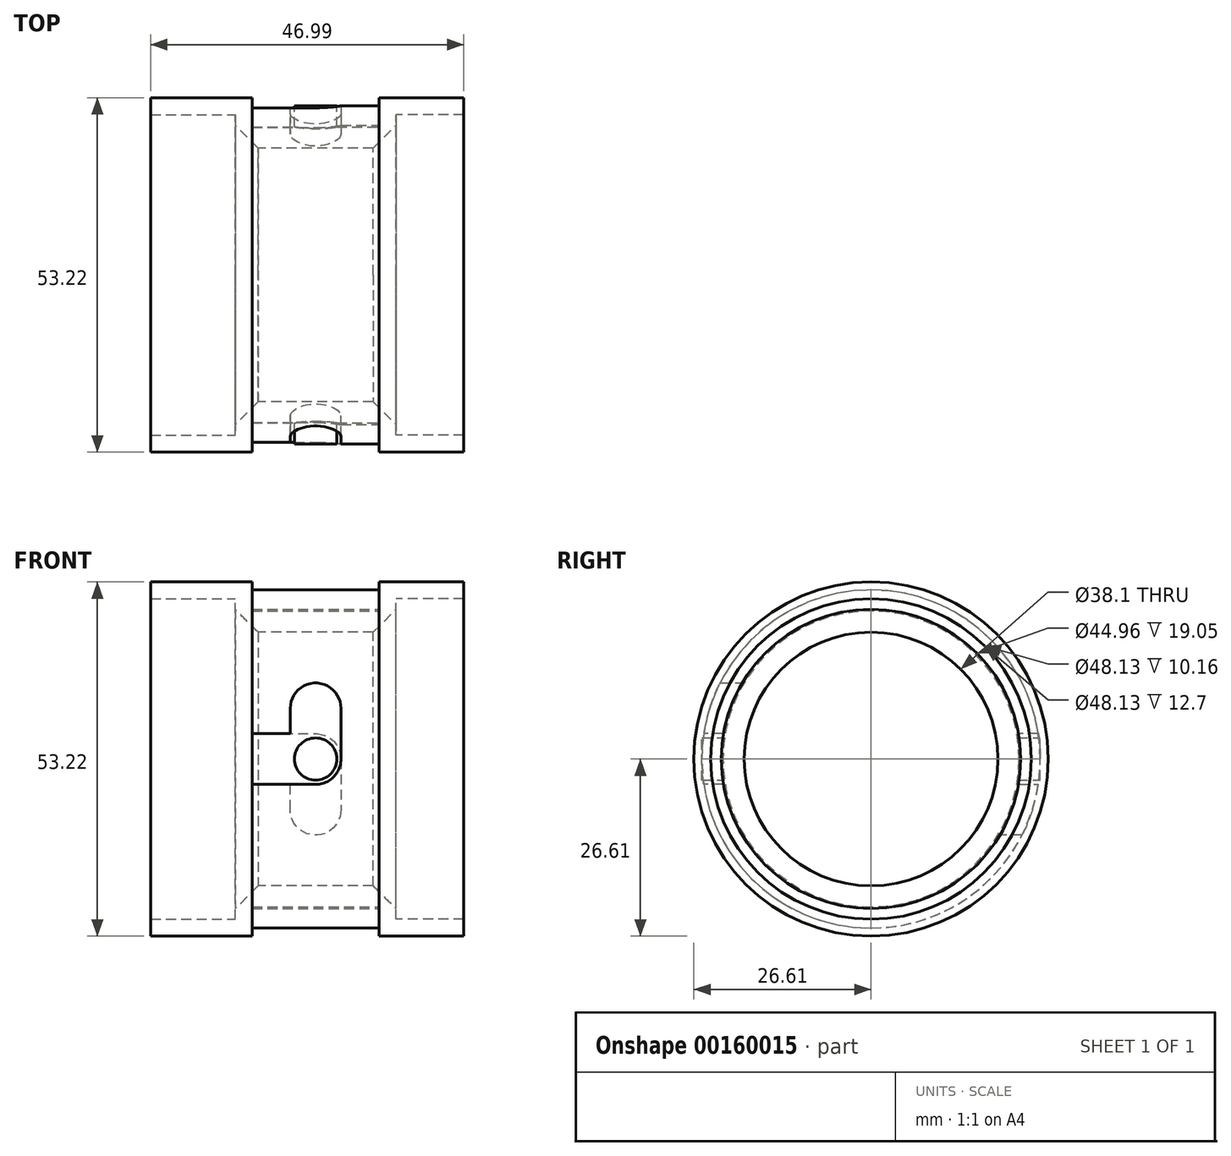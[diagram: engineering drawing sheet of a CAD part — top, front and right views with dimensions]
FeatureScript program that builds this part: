
annotation { "Feature Type Name" : "Feature", "Feature Type Description" : "" }
export const myFeature = defineFeature(function(context is Context, id is Id, definition is map)
    precondition{}
    {
        {
            var Q0;
            Q0=qCreatedBy(makeId("Right.planeOp"),FACE);
            var sketch = newSketch(context, id + "F0", { "sketchPlane" : qUnion([Q0])});
            skCircle(sketch, "E0", {"center": v(0, 0) * mm, "radius": 24.07 * mm});
            skCircle(sketch, "E1", {"center": v(0, 0) * mm, "radius": 26.6 * mm});
            skCircle(sketch, "E2", {"center": v(0, 0) * mm, "radius": 19.05 * mm});
            skSolve(sketch);
        }
        {
            var Q0;
            Q0=makeQuery(id+"F0.imprint","IMPRINT",FACE,{"disambiguationData":[TD([[makeQuery(id+"F0.imprint","IMPRINT",EDGE,{"derivedFrom":sQuery(id+"F0.wireOp",EDGE,"E0")}),-1.0]])]});
            var Q1;
            Q1=makeQuery(id+"F0.imprint","IMPRINT",FACE,{"disambiguationData":[TD([[makeQuery(id+"F0.imprint","IMPRINT",EDGE,{"derivedFrom":sQuery(id+"F0.wireOp",EDGE,"E0")}),1.0]])]});
            extrude(context, id + "F1", {"entities" : qUnion([Q0, Q1]), "depth" : 2.54 * mm});
        }
        {
            var Q0;
            Q0=makeQuery(id+"F0.imprint","IMPRINT",FACE,{"disambiguationData":[TD([[makeQuery(id+"F0.imprint","IMPRINT",EDGE,{"derivedFrom":sQuery(id+"F0.wireOp",EDGE,"E0")}),-1.0]])]});
            extrude(context, id + "F2", {"entities" : qUnion([Q0]), "operationType" : NewBodyOperationType.ADD, "depth" : 12.7 * mm});
        }
        {
            var Q0;
            Q0=qCreatedBy(makeId("Right.planeOp"),FACE);
            var sketch = newSketch(context, id + "F3", { "sketchPlane" : qUnion([Q0])});
            skCircle(sketch, "E3", {"center": v(0, 0) * mm, "radius": 22.48 * mm});
            skCircle(sketch, "E4", {"center": v(0, 0) * mm, "radius": 25.4 * mm});
            skSolve(sketch);
        }
        {
            var Q0;
            Q0 = qSketchRegion(id + "F3", true);
            extrude(context, id + "F4", {"entities" : qUnion([Q0]), "operationType" : NewBodyOperationType.ADD, "oppositeDirection" : true, "offsetDistance" : 25.4 * mm, "depth" : 19.05 * mm});
        }
        {
            var Q0;
            Q0=qCreatedBy(makeId("Front.planeOp"),FACE);
            var sketch = newSketch(context, id + "F5", { "sketchPlane" : qUnion([Q0])});
            skLineSegment(sketch, "E5", {"start": v(0, 0) * mm, "end": v(-19.05, 0) * mm, "construction": true});
            skLineSegment(sketch, "E6", {"start": v(-19.05, -3.81) * mm, "end": v(-19.05, 3.8) * mm});
            skLineSegment(sketch, "E7", {"start": v(-19.05, 3.8) * mm, "end": v(-9.53, 3.8) * mm});
            skLineSegment(sketch, "E8", {"start": v(-9.53, 3.8) * mm, "end": v(-9.52, -3.8) * mm});
            skLineSegment(sketch, "E9", {"start": v(-9.52, -3.81) * mm, "end": v(-19.05, -3.81) * mm});
            skSolve(sketch);
        }
        {
            var Q0;
            Q0=qSketchRegion(id+"F5",true);
            extrude(context, id + "F6", {"entities" : qUnion([Q0]), "operationType" : NewBodyOperationType.REMOVE, "oppositeDirection" : true, "depth" : 50.8 * mm, "hasSecondDirection" : true, "secondDirectionOppositeDirection" : false, "secondDirectionDepth" : 50.8 * mm});
        }
        {
            var Q0;
            Q0=qCreatedBy(makeId("Front.planeOp"),FACE);
            var sketch = newSketch(context, id + "F7", { "sketchPlane" : qUnion([Q0])});
            skLineSegment(sketch, "E10", {"start": v(0, 0) * mm, "end": v(-9.53, 0) * mm, "construction": true});
            skCircle(sketch, "E11", {"center": v(-9.53, 0) * mm, "radius": 3.81 * mm});
            skSolve(sketch);
        }
        {
            var Q0;
            Q0=qSketchRegion(id+"F7",true);
            extrude(context, id + "F8", {"entities" : qUnion([Q0]), "operationType" : NewBodyOperationType.REMOVE, "oppositeDirection" : true, "depth" : 50.8 * mm, "hasSecondDirection" : true, "secondDirectionOppositeDirection" : false, "secondDirectionDepth" : 50.8 * mm});
        }
        {
            var Q0;
            Q0=qCreatedBy(makeId("Front.planeOp"),FACE);
            var sketch = newSketch(context, id + "F9", { "sketchPlane" : qUnion([Q0])});
            skLineSegment(sketch, "E12", {"start": v(0, 0) * mm, "end": v(-9.53, 0) * mm, "construction": true});
            skLineSegment(sketch, "E13", {"start": v(-9.53, 0) * mm, "end": v(-9.53, 7.62) * mm, "construction": true});
            skCircle(sketch, "E14", {"center": v(-9.53, 7.62) * mm, "radius": 3.81 * mm});
            skLineSegment(sketch, "E15", {"start": v(-9.53, 7.62) * mm, "end": v(-13.34, 7.62) * mm, "construction": true});
            skLineSegment(sketch, "E16", {"start": v(-13.34, 7.62) * mm, "end": v(-13.34, 0) * mm});
            skLineSegment(sketch, "E17", {"start": v(-13.34, 0) * mm, "end": v(-5.72, 0) * mm});
            skLineSegment(sketch, "E18", {"start": v(-5.72, 0) * mm, "end": v(-5.72, 7.62) * mm});
            skSolve(sketch);
        }
        {
            var Q0;
            {var subQ0=sQuery(id+"F9.wireOp",EDGE,"E14");var subQ1=makeQuery(id+"F9.imprint","INTERSECT",VERTEX,{"derivedFrom":[subQ0,sQuery(id+"F9.wireOp",EDGE,"E16")]});Q0=makeQuery(id+"F9.imprint","IMPRINT",FACE,{"disambiguationData":[TD([[makeQuery(id+"F9.imprint","IMPRINT",EDGE,{"disambiguationData":[TD([[subQ1,1.0]])],"derivedFrom":subQ0}),1.0]])]});}
            var Q1;
            {var subQ0=sQuery(id+"F9.wireOp",EDGE,"E16");Q1=makeQuery(id+"F9.imprint","IMPRINT",FACE,{"disambiguationData":[TD([[makeQuery(id+"F9.imprint","IMPRINT",EDGE,{"derivedFrom":subQ0}),1.0]])]});}
            var Q2;
            Q2=sQuery(id+"F9.wireOp",EDGE,"E15");
            extrude(context, id + "F10", {"entities" : qUnion([Q0, Q1]), "operationType" : NewBodyOperationType.REMOVE, "surfaceEntities" : qUnion([Q2]), "depth" : 50.8 * mm});
        }
        {
            var Q0;
            Q0=qCreatedBy(makeId("Front.planeOp"),FACE);
            var sketch = newSketch(context, id + "F11", { "sketchPlane" : qUnion([Q0])});
            skLineSegment(sketch, "E19", {"start": v(0, 0) * mm, "end": v(-9.53, 0) * mm, "construction": true});
            skLineSegment(sketch, "E20", {"start": v(-9.53, 0) * mm, "end": v(-9.53, -7.62) * mm, "construction": true});
            skCircle(sketch, "E21", {"center": v(-9.53, -7.62) * mm, "radius": 3.81 * mm});
            skLineSegment(sketch, "E22", {"start": v(-9.53, -7.62) * mm, "end": v(-13.33, -7.62) * mm, "construction": true});
            skLineSegment(sketch, "E23", {"start": v(-13.33, -7.62) * mm, "end": v(-13.33, 0) * mm});
            skLineSegment(sketch, "E24", {"start": v(-13.33, 0) * mm, "end": v(-5.72, 0) * mm});
            skLineSegment(sketch, "E25", {"start": v(-5.71, 0) * mm, "end": v(-5.71, -7.62) * mm});
            skSolve(sketch);
        }
        {
            var Q0;
            {var subQ0=sQuery(id+"F11.wireOp",EDGE,"E23");Q0=makeQuery(id+"F11.imprint","IMPRINT",FACE,{"disambiguationData":[TD([[makeQuery(id+"F11.imprint","IMPRINT",EDGE,{"derivedFrom":subQ0}),-1.0]])]});}
            var Q1;
            {var subQ0=sQuery(id+"F11.wireOp",EDGE,"E21");var subQ1=makeQuery(id+"F11.imprint","INTERSECT",VERTEX,{"derivedFrom":[subQ0,sQuery(id+"F11.wireOp",EDGE,"E23")]});Q1=makeQuery(id+"F11.imprint","IMPRINT",FACE,{"disambiguationData":[TD([[makeQuery(id+"F11.imprint","IMPRINT",EDGE,{"disambiguationData":[TD([[subQ1,1.0]])],"derivedFrom":subQ0}),1.0]])]});}
            var Q2;
            Q2=sQuery(id+"F11.wireOp",EDGE,"E22");
            extrude(context, id + "F12", {"entities" : qUnion([Q0, Q1]), "operationType" : NewBodyOperationType.REMOVE, "surfaceEntities" : qUnion([Q2]), "oppositeDirection" : true, "depth" : 25.4 * mm});
        }
        {
            var Q0;
            Q0=qCreatedBy(makeId("Right.planeOp"),FACE);
            var sketch = newSketch(context, id + "F13", { "sketchPlane" : qUnion([Q0])});
            skCircle(sketch, "E26", {"center": v(0, 0) * mm, "radius": 19.05 * mm});
            skCircle(sketch, "E27", {"center": v(0, 0) * mm, "radius": 22.23 * mm});
            skCircle(sketch, "E28", {"center": v(0, 0) * mm, "radius": 24.07 * mm});
            skSolve(sketch);
        }
        {
            var Q0;
            Q0=makeQuery(id+"F13.imprint","IMPRINT",FACE,{"disambiguationData":[TD([[makeQuery(id+"F13.imprint","IMPRINT",EDGE,{"derivedFrom":sQuery(id+"F13.wireOp",EDGE,"E26")}),-1.0]])]});
            extrude(context, id + "F14", {"entities" : qUnion([Q0]), "oppositeDirection" : true, "depth" : 21.59 * mm});
        }
        {
            var Q0;
            Q0=makeQuery(id+"F13.imprint","IMPRINT",FACE,{"disambiguationData":[TD([[makeQuery(id+"F13.imprint","IMPRINT",EDGE,{"derivedFrom":sQuery(id+"F13.wireOp",EDGE,"E27")}),-1.0]])]});
            extrude(context, id + "F15", {"entities" : qUnion([Q0]), "operationType" : NewBodyOperationType.ADD, "oppositeDirection" : true, "depth" : 21.59 * mm, "hasSecondDirection" : true, "secondDirectionOppositeDirection" : true, "secondDirectionDepth" : 19.05 * mm});
        }
        {
            var Q0;
            Q0=qCreatedBy(makeId("Right.planeOp"),FACE);
            var sketch = newSketch(context, id + "F16", { "sketchPlane" : qUnion([Q0])});
            skCircle(sketch, "E29", {"center": v(0, 0) * mm, "radius": 24.07 * mm});
            skCircle(sketch, "E30", {"center": v(0, 0) * mm, "radius": 26.6 * mm});
            skSolve(sketch);
        }
        {
            var Q0;
            Q0=qSketchRegion(id+"F16",true);
            extrude(context, id + "F17", {"entities" : qUnion([Q0]), "operationType" : NewBodyOperationType.ADD, "oppositeDirection" : true, "depth" : 34.3 * mm, "hasSecondDirection" : true, "secondDirectionOppositeDirection" : true, "secondDirectionDepth" : 19.05 * mm});
        }
        {
            var Q0;
            Q0=qCreatedBy(makeId("Front.planeOp"),FACE);
            var sketch = newSketch(context, id + "F18", { "sketchPlane" : qUnion([Q0])});
            skLineSegment(sketch, "E31", {"start": v(0, 0) * mm, "end": v(-9.52, 0) * mm, "construction": true});
            skCircle(sketch, "E32", {"center": v(-9.52, 0) * mm, "radius": 3.18 * mm});
            skSolve(sketch);
        }
        {
            var Q0;
            Q0=qSketchRegion(id+"F18",true);
            extrude(context, id + "F19", {"entities" : qUnion([Q0]), "operationType" : NewBodyOperationType.ADD, "depth" : 25.4 * mm, "hasSecondDirection" : true, "secondDirectionOppositeDirection" : true, "secondDirectionDepth" : 25.4 * mm});
        }
        {
            var Q0;
            Q0=makeQuery(id+"F13.imprint","IMPRINT",FACE,{"disambiguationData":[TD([[makeQuery(id+"F13.imprint","IMPRINT",EDGE,{"derivedFrom":sQuery(id+"F13.wireOp",EDGE,"E26")}),1.0]])]});
            extrude(context, id + "F20", {"entities" : qUnion([Q0]), "operationType" : NewBodyOperationType.REMOVE, "oppositeDirection" : true, "depth" : 25.4 * mm});
        }
        {
            var Q0;
            Q0=qCreatedBy(makeId("Front.planeOp"),FACE);
            var sketch = newSketch(context, id + "F21", { "sketchPlane" : qUnion([Q0])});
            skLineSegment(sketch, "E33", {"start": v(0, 0) * mm, "end": v(24.47, 0) * mm, "construction": true});
            skLineSegment(sketch, "E34", {"start": v(0, 0) * mm, "end": v(0, -22.48) * mm, "construction": true});
            skLineSegment(sketch, "E35", {"start": v(0, 0) * mm, "end": v(0, -19.94) * mm, "construction": true});
            skLineSegment(sketch, "E36", {"start": v(0, -22.48) * mm, "end": v(2.54, -22.48) * mm, "construction": true});
            skLineSegment(sketch, "E37", {"start": v(2.54, -22.48) * mm, "end": v(2.54, -19.94) * mm});
            skLineSegment(sketch, "E38", {"start": v(2.54, -19.94) * mm, "end": v(0, -19.94) * mm});
            skLineSegment(sketch, "E39", {"start": v(0, -19.94) * mm, "end": v(2.54, -22.48) * mm});
            skLineSegment(sketch, "E40", {"start": v(0, -19.94) * mm, "end": v(0, -19.05) * mm});
            skLineSegment(sketch, "E41", {"start": v(0, -19.05) * mm, "end": v(2.54, -19.05) * mm});
            skLineSegment(sketch, "E42", {"start": v(2.54, -19.05) * mm, "end": v(2.54, -19.94) * mm});
            skLineSegment(sketch, "E43", {"start": v(0, -19.94) * mm, "end": v(-0.89, -19.05) * mm});
            skLineSegment(sketch, "E44", {"start": v(-0.89, -19.05) * mm, "end": v(0, -19.05) * mm});
            skLineSegment(sketch, "E45", {"start": v(0, -19.05) * mm, "end": v(0, -19.94) * mm});
            skSolve(sketch);
        }
        {
            var Q0;
            Q0=qSketchRegion(id+"F21",true);
            var Q1;
            Q1=sQuery(id+"F21.wireOp",EDGE,"E33");
            revolve(context, id + "F22", {"operationType" : NewBodyOperationType.REMOVE, "entities" : qUnion([Q0]), "axis" : qUnion([Q1]), "revolveType" : RevolveType.FULL, "oppositeDirection" : true});
        }
        {
            var Q0;
            Q0=qCreatedBy(makeId("Front.planeOp"),FACE);
            var sketch = newSketch(context, id + "F23", { "sketchPlane" : qUnion([Q0])});
            skLineSegment(sketch, "E46", {"start": v(0, 0) * mm, "end": v(-21.59, 0) * mm, "construction": true});
            skLineSegment(sketch, "E47", {"start": v(-21.59, 0) * mm, "end": v(-21.59, -19.05) * mm, "construction": true});
            skLineSegment(sketch, "E48", {"start": v(-21.59, -19.05) * mm, "end": v(-21.59, -22.48) * mm});
            skLineSegment(sketch, "E49", {"start": v(-21.59, -22.48) * mm, "end": v(-18.16, -19.05) * mm});
            skLineSegment(sketch, "E50", {"start": v(-18.16, -19.05) * mm, "end": v(-21.59, -19.05) * mm});
            skSolve(sketch);
        }
        {
            var Q0;
            Q0=makeQuery(id+"F23.imprint","IMPRINT",FACE,{"disambiguationData":[TD([[makeQuery(id+"F23.imprint","IMPRINT",EDGE,{"derivedFrom":sQuery(id+"F23.wireOp",EDGE,"E48")}),1.0]])]});
            var Q1;
            Q1=sQuery(id+"F23.wireOp",EDGE,"E46");
            revolve(context, id + "F24", {"operationType" : NewBodyOperationType.REMOVE, "entities" : qUnion([Q0]), "axis" : qUnion([Q1]), "revolveType" : RevolveType.FULL, "oppositeDirection" : true});
        }
        {
            var Q0;
            Q0=qSketchRegion(id+"F21",true);
            var Q1;
            Q1=sQuery(id+"F21.wireOp",EDGE,"E33");
            revolve(context, id + "F25", {"operationType" : NewBodyOperationType.REMOVE, "entities" : qUnion([Q0]), "axis" : qUnion([Q1]), "revolveType" : RevolveType.FULL, "oppositeDirection" : true});
        }
    });
